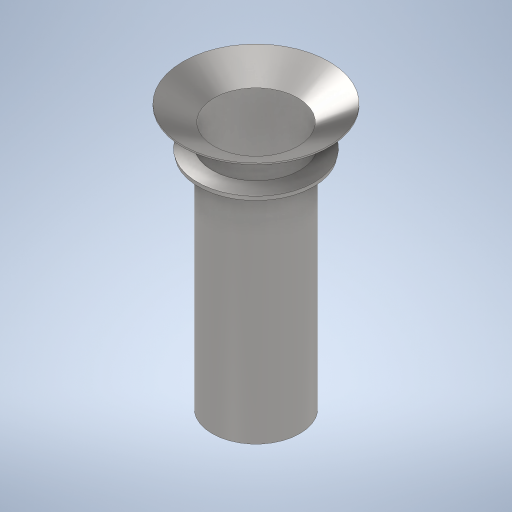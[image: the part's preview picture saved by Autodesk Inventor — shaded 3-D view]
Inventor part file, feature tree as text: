
AUTODESK INVENTOR PART (.ipt)
format: ipt  version: 2023 (Build 270158000, 158)  size: 283,648 bytes
history: native  units: in
note: dims shown in document units (in); Inventor stores cm internally (conversion verified against a paired STEP export)
features: sketch x3, extrude x2, other x1, plane x1, revolve x1, projected_geometry x1
ambient origin geometry x8: Origin, YZ Plane, XZ Plane, XY Plane, X Axis, Y Axis, Z Axis, Center Point
bodies: Solid1 (feature_tree)
feature tree (9):
  sketch  "Sketch1"  dims[d0=12.0in d1=0.25in]
  extrude  "Extrusion1"  Depth=0.25in
  extrude  "Extrusion2"  Depth=0.25in TaperAngle=0.0deg
  other  "Work Axis1"
  sketch  "Sketch2"  dims[d2=34.0in d3=0.0in d4=0.25in d5=0.0in]
  plane  "Work Plane1"
  revolve  "Revolution1"  [1 undecoded]
  sketch  "Sketch3"  dims[d6=2.2in d7=4.0in d8=0.2in d9=360.0deg]
  projected_geometry  "Projected Loop1"
note: 1 required parameter value undecoded (feature->parameter linkage not recoverable at this tier; creation-order binding heuristic only, values carry confidence <= 0.55)
